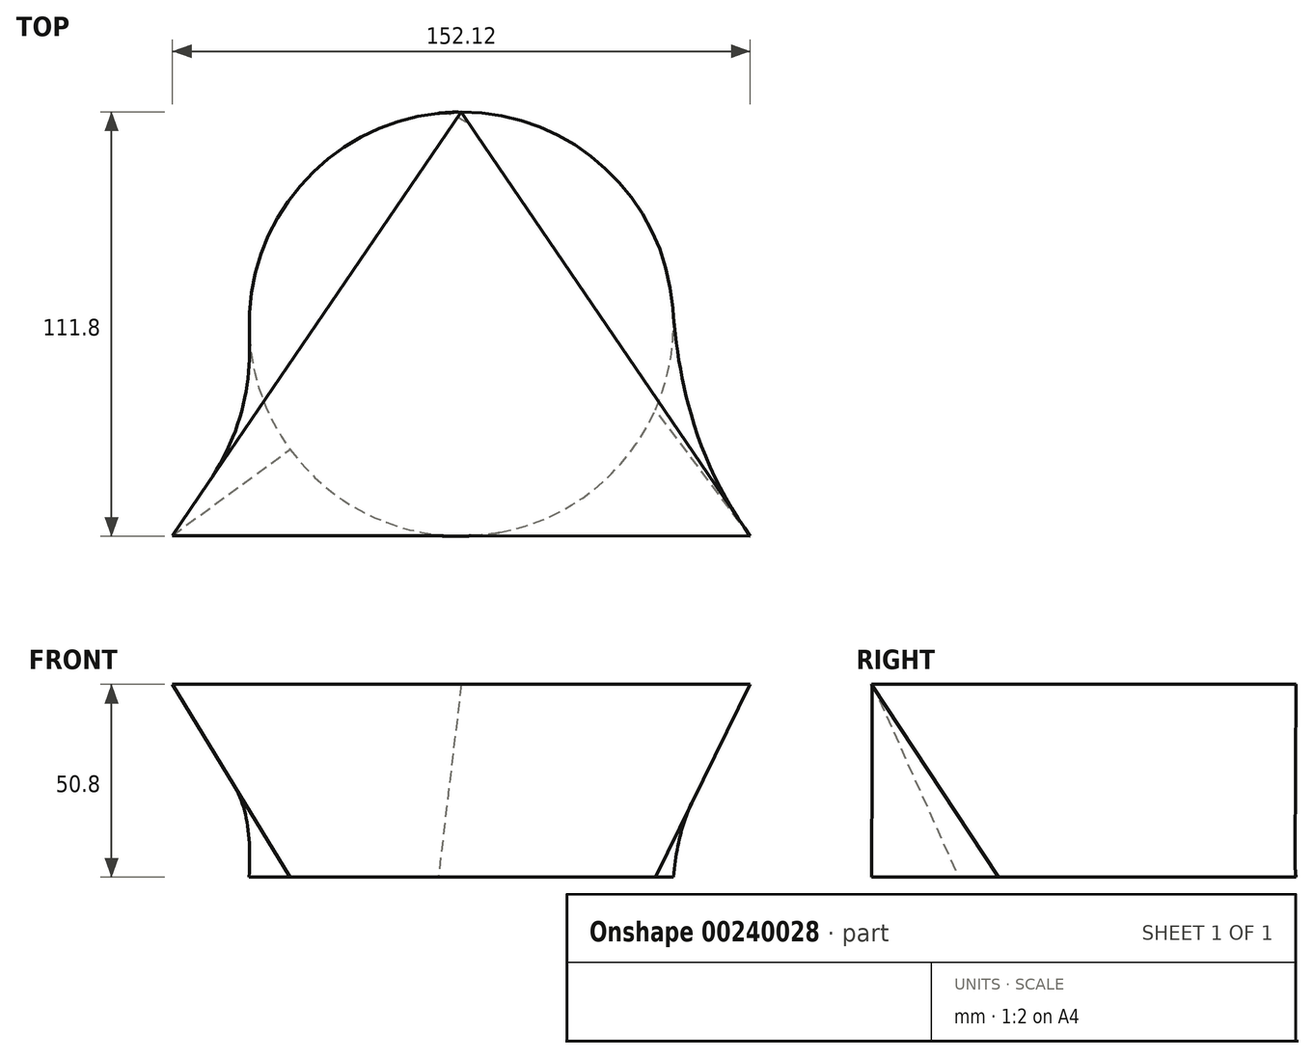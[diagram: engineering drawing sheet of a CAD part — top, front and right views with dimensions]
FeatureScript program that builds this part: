
annotation { "Feature Type Name" : "Feature", "Feature Type Description" : "" }
export const myFeature = defineFeature(function(context is Context, id is Id, definition is map)
    precondition{}
    {
        {
            var Q0;
            Q0=qCreatedBy(makeId("Top.planeOp"),FACE);
            var sketch = newSketch(context, id + "F0", { "sketchPlane" : qUnion([Q0])});
            skCircle(sketch, "E0", {"center": v(0, 0) * mm, "radius": 55.86 * mm});
            skSolve(sketch);
        }
        {
            var Q0;
            Q0=qCreatedBy(makeId("Top.planeOp"),FACE);
            cPlane(context, id + "F1", {"entities" : qUnion([Q0]), "cplaneType" : CPlaneType.OFFSET, "offset" : 50.8 * mm, "width" : 152.4 * mm, "height" : 152.4 * mm});
        }
        {
            var Q0;
            Q0=qCreatedBy(id+"F1.planeOp",FACE);
            var sketch = newSketch(context, id + "F2", { "sketchPlane" : qUnion([Q0])});
            skLineSegment(sketch, "E1", {"start": v(-76.06, -55.7) * mm, "end": v(0, 55.9) * mm});
            skLineSegment(sketch, "E2", {"start": v(0, 55.9) * mm, "end": v(76.06, -55.9) * mm});
            skLineSegment(sketch, "E3", {"start": v(76.06, -55.9) * mm, "end": v(-76.06, -55.7) * mm});
            skSolve(sketch);
        }
        {
            var Q0;
            Q0=makeQuery(id+"F2.imprint","IMPRINT",FACE,{"disambiguationData":[TD([[makeQuery(id+"F2.imprint","IMPRINT",EDGE,{"derivedFrom":sQuery(id+"F2.wireOp",EDGE,"E1")}),-1.0]])]});
            var Q1;
            Q1=makeQuery(id+"F0.imprint","IMPRINT",FACE,{"disambiguationData":[TD([[makeQuery(id+"F0.imprint","IMPRINT",EDGE,{"derivedFrom":sQuery(id+"F0.wireOp",EDGE,"E0")}),1.0]])]});
            loft(context, id + "F3", {"sheetProfilesArray" : [{ "sheetProfileEntities" : qUnion([Q0]) }, { "sheetProfileEntities" : qUnion([Q1]) }]});
        }
    });
